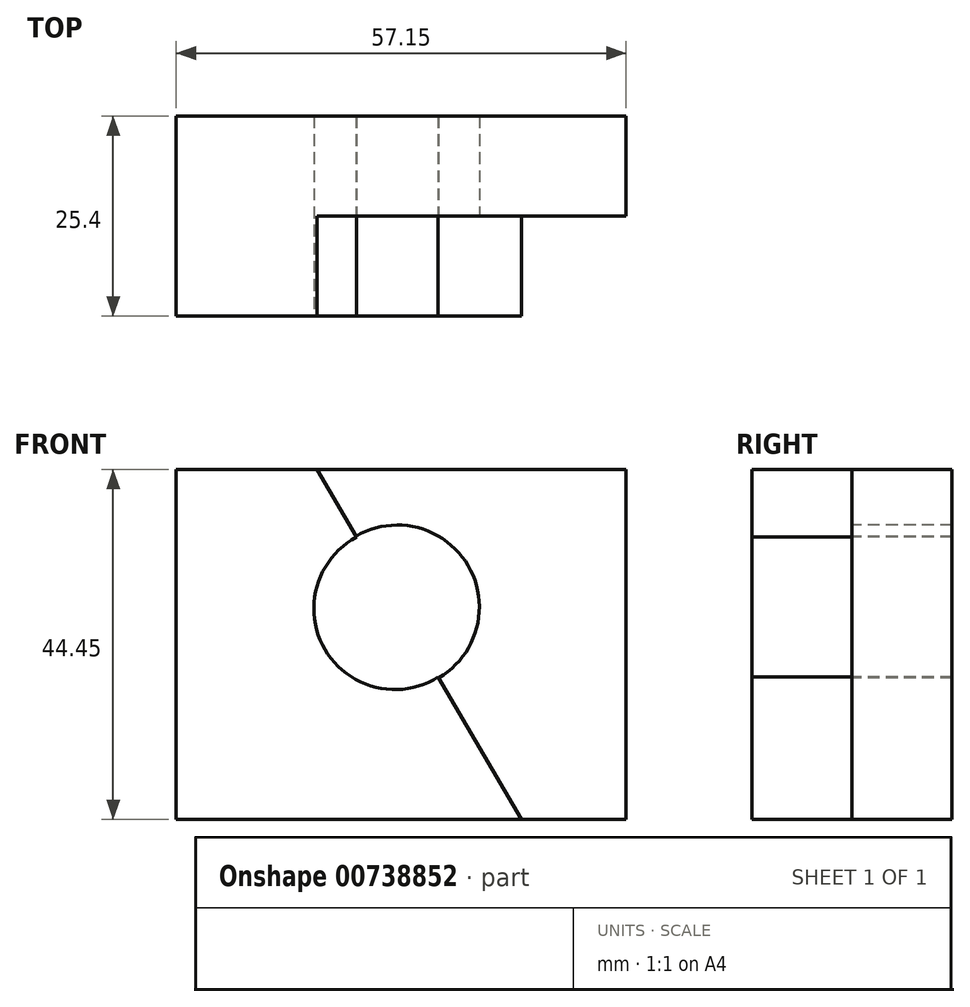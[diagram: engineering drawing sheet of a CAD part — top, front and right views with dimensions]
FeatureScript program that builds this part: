
annotation { "Feature Type Name" : "Feature", "Feature Type Description" : "" }
export const myFeature = defineFeature(function(context is Context, id is Id, definition is map)
    precondition{}
    {
        {
            var Q0;
            Q0=qCreatedBy(makeId("Front.planeOp"),FACE);
            var sketch = newSketch(context, id + "F0", { "sketchPlane" : qUnion([Q0])});
            skLineSegment(sketch, "E0", {"start": v(0, 0) * mm, "end": v(57.15, 0) * mm});
            skLineSegment(sketch, "E1", {"start": v(57.15, 0) * mm, "end": v(57.15, 44.45) * mm});
            skLineSegment(sketch, "E2", {"start": v(57.15, 44.45) * mm, "end": v(0, 44.45) * mm});
            skLineSegment(sketch, "E3", {"start": v(0, 44.45) * mm, "end": v(0, 0) * mm});
            skSolve(sketch);
        }
        {
            var Q0;
            Q0=makeQuery(id+"F0.imprint","IMPRINT",FACE,{"disambiguationData":[TD([[makeQuery(id+"F0.imprint","IMPRINT",EDGE,{"derivedFrom":sQuery(id+"F0.wireOp",EDGE,"E0")}),1.0]])]});
            extrude(context, id + "F1", {"entities" : qUnion([Q0]), "depth" : 25.4 * mm, "offsetDistance" : 25.4 * mm});
        }
        {
            var Q0;
            Q0=makeQuery(id+"F1.opExtrude","CAP_FACE",FACE,{"disambiguationData":[OSD([sQuery(id+"F0.wireOp",EDGE,"E0"),sQuery(id+"F0.wireOp",EDGE,"E1"),sQuery(id+"F0.wireOp",EDGE,"E2"),sQuery(id+"F0.wireOp",EDGE,"E3")])],"isStart":false});
            var sketch = newSketch(context, id + "F2", { "sketchPlane" : qUnion([Q0])});
            skLineSegment(sketch, "E4", {"start": v(17.87, 44.45) * mm, "end": v(43.85, 0) * mm});
            skLineSegment(sketch, "E5", {"start": v(43.85, 0) * mm, "end": v(57.15, 0) * mm});
            skLineSegment(sketch, "E6", {"start": v(57.15, 0) * mm, "end": v(57.15, 44.45) * mm});
            skLineSegment(sketch, "E7", {"start": v(57.15, 44.45) * mm, "end": v(17.87, 44.45) * mm});
            skSolve(sketch);
        }
        {
            var Q0;
            Q0 = qSketchRegion(id + "F2", true);
            extrude(context, id + "F3", {"entities" : qUnion([Q0]), "operationType" : NewBodyOperationType.REMOVE, "oppositeDirection" : true, "depth" : 12.7 * mm, "offsetDistance" : 25.4 * mm});
        }
        {
            var Q0;
            Q0=makeQuery(id+"F3.boolean.opBoolean","COPY",FACE,{"derivedFrom":makeQuery(id+"F3.opExtrude","CAP_FACE",FACE,{"disambiguationData":[OSD([sQuery(id+"F2.wireOp",EDGE,"E4"),sQuery(id+"F2.wireOp",EDGE,"E5"),sQuery(id+"F2.wireOp",EDGE,"E6"),sQuery(id+"F2.wireOp",EDGE,"E7")])],"isStart":false})});
            var sketch = newSketch(context, id + "F4", { "sketchPlane" : qUnion([Q0])});
            skCircle(sketch, "E8", {"center": v(28.08, 26.97) * mm, "radius": 10.42 * mm});
            skSolve(sketch);
        }
        {
            var Q0;
            {var subQ0=sQuery(id+"F4.wireOp",EDGE,"E8");var subQ1=makeQuery(id+"F3.boolean.opBoolean","COPY",EDGE,{"derivedFrom":makeQuery(id+"F3.opExtrude","CAP_EDGE",EDGE,{"disambiguationData":[OSD([sQuery(id+"F2.wireOp",EDGE,"E4")])],"isStart":false})});var subQ2=makeQuery(id+"F4.imprint","INTERSECT",VERTEX,{"disambiguationData":[OD(0.0)],"derivedFrom":[subQ1,subQ0]});Q0=makeQuery(id+"F4.imprint","IMPRINT",FACE,{"disambiguationData":[TD([[makeQuery(id+"F4.imprint","IMPRINT",EDGE,{"disambiguationData":[TD([[subQ2,1.0]])],"derivedFrom":subQ0}),1.0]])]});}
            extrude(context, id + "F5", {"entities" : qUnion([Q0]), "operationType" : NewBodyOperationType.REMOVE, "endBound" : BoundingType.THROUGH_ALL, "oppositeDirection" : true, "depth" : 25.4 * mm, "offsetDistance" : 25.4 * mm});
        }
        {
            var Q0;
            Q0=makeQuery(id+"F1.opExtrude","CAP_FACE",FACE,{"disambiguationData":[OSD([sQuery(id+"F0.wireOp",EDGE,"E0"),sQuery(id+"F0.wireOp",EDGE,"E1"),sQuery(id+"F0.wireOp",EDGE,"E2"),sQuery(id+"F0.wireOp",EDGE,"E3")])],"isStart":false});
            var sketch = newSketch(context, id + "F6", { "sketchPlane" : qUnion([Q0])});
            skArc(sketch, "E9", {"start": v(22.9, 35.86) * mm, "mid": v(18.89, 21.6) * mm, "end": v(33.28, 18.08) * mm});
            skSolve(sketch);
        }
        {
            var Q0;
            {var subQ0=sQuery(id+"F6.wireOp",EDGE,"E9");Q0=makeQuery(id+"F6.imprint","IMPRINT",FACE,{"disambiguationData":[TD([[makeQuery(id+"F6.imprint","IMPRINT",EDGE,{"derivedFrom":subQ0}),1.0]])]});}
            extrude(context, id + "F7", {"entities" : qUnion([Q0]), "operationType" : NewBodyOperationType.REMOVE, "endBound" : BoundingType.THROUGH_ALL, "oppositeDirection" : true, "depth" : 25.4 * mm, "offsetDistance" : 25.4 * mm});
        }
    });
